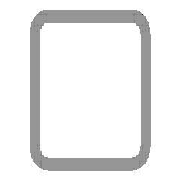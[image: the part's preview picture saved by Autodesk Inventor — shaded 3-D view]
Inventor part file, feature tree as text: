
AUTODESK INVENTOR PART (.ipt)
format: ipt  version: 2021 (Build 250183000, 183)  size: 130,048 bytes
history: native  units: mm (DEFAULTED — no unit token found)
features: other x4, sketch x3, extrude x1, plane x1
ambient origin geometry x8: Origin, YZ Plane, XZ Plane, XY Plane, X Axis, Y Axis, Z Axis, Center Point
bodies: Solid1 (feature_tree)
feature tree (9):
  parser-record x1  (decoder bookkeeping rows leaked as tree rows — omitted from the tree; the rows remain in map.json)
  other  "Driven Length"
  other  "Plano inicial"
  other  "Plano final"
  extrude  "Corpo"  TaperAngle=0.0deg  [1 undecoded]
  sketch  "Esboço"  dims[d11=50.8mm d12=4.7625mm d13=-0.0mm d14=2000.0mm d15=25.4mm d16=25.4mm d17=9.525mm d18=90.0deg d19=2000.0mm]
  sketch  "Sketch3"  dims[d3=2000.0mm d4=0.0mm]
  plane  "Work Plane3"
  sketch  "Sketch4"  dims[d10=50.8mm]
note: 1 required parameter value undecoded (feature->parameter linkage not recoverable at this tier; creation-order binding heuristic only, values carry confidence <= 0.55)
